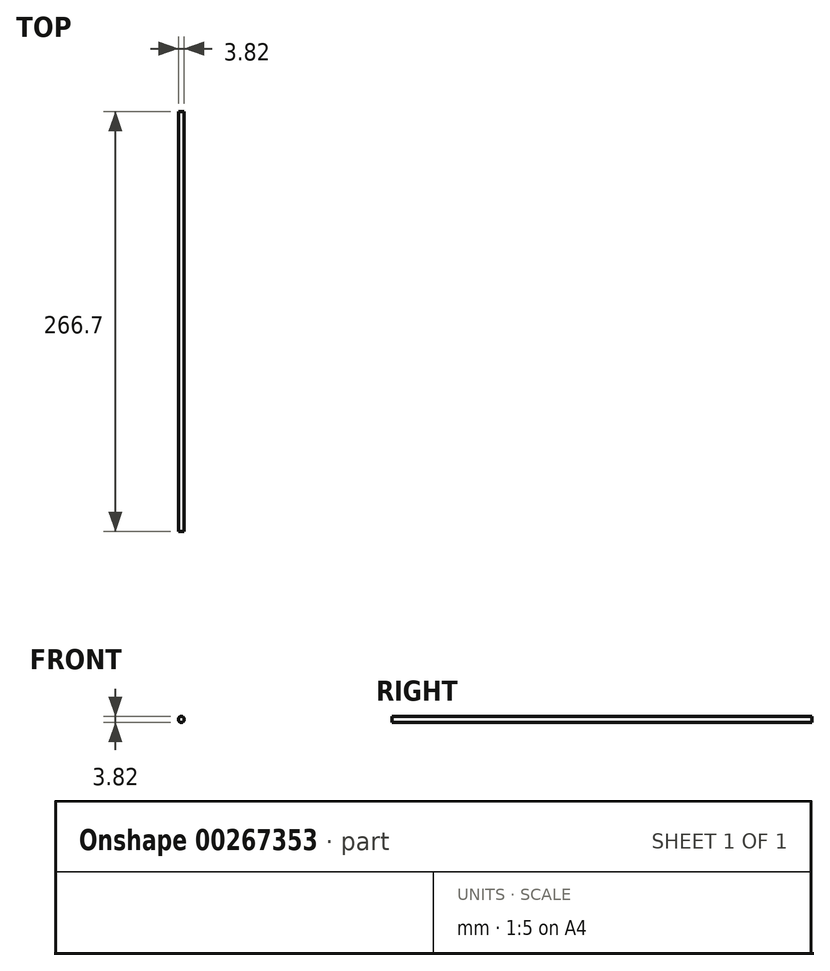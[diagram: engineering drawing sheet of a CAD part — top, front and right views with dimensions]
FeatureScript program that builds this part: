
annotation { "Feature Type Name" : "Feature", "Feature Type Description" : "" }
export const myFeature = defineFeature(function(context is Context, id is Id, definition is map)
    precondition{}
    {
        {
            var Q0;
            Q0=qCreatedBy(makeId("Front.planeOp"),FACE);
            var sketch = newSketch(context, id + "F0", { "sketchPlane" : qUnion([Q0])});
            skCircle(sketch, "E0", {"center": v(0, 0) * mm, "radius": 1.9 * mm});
            skSolve(sketch);
        }
        {
            var Q0;
            Q0 = qSketchRegion(id + "F0", true);
            extrude(context, id + "F1", {"entities" : qUnion([Q0]), "depth" : 266.7 * mm});
        }
    });
